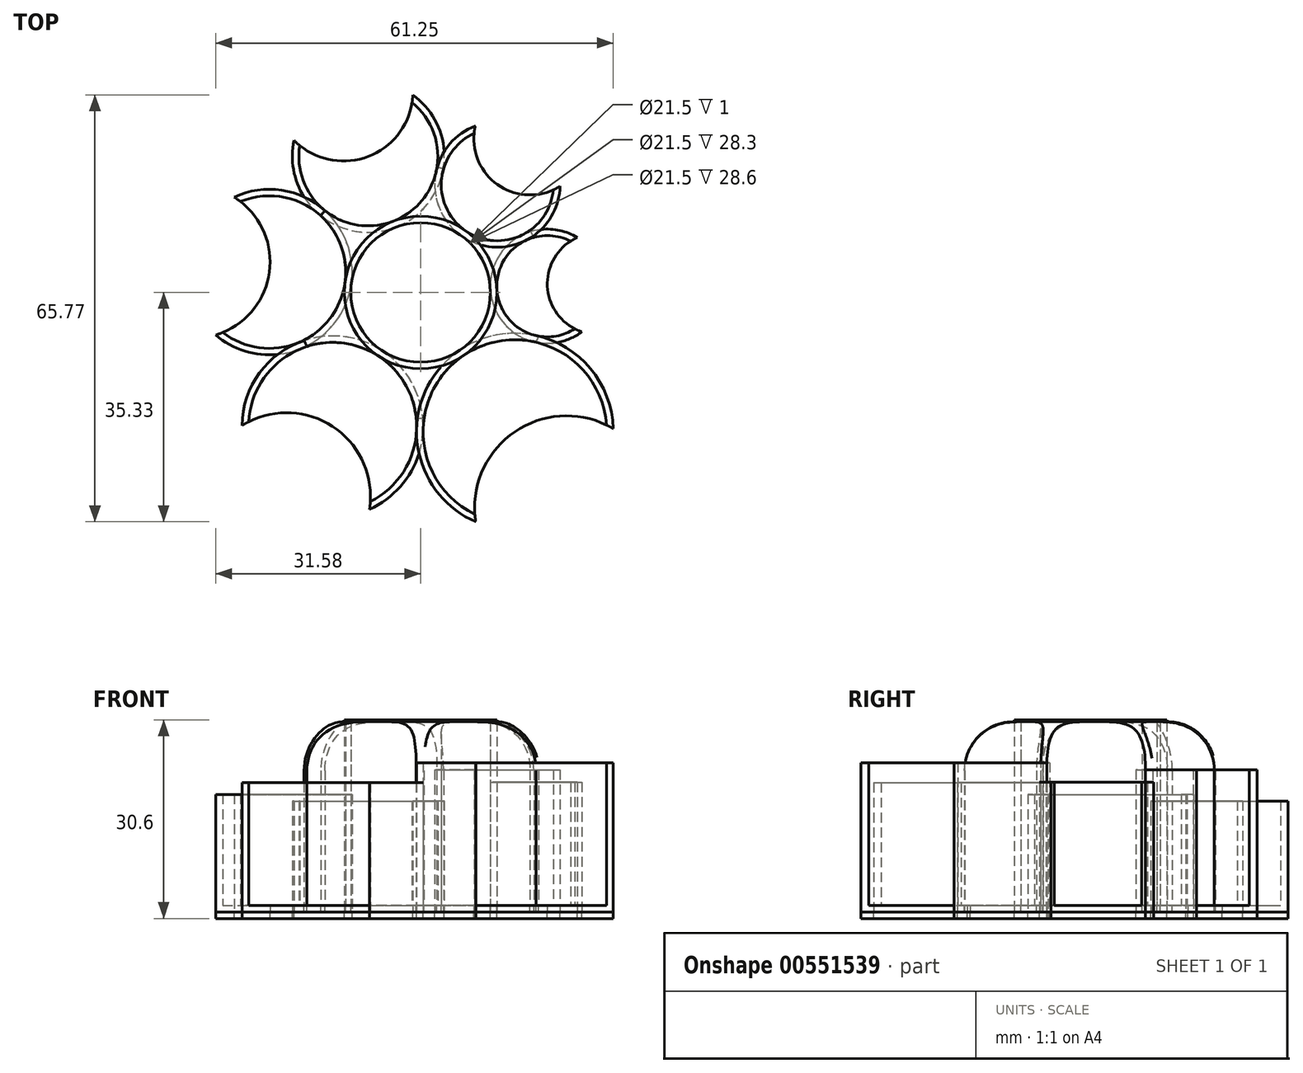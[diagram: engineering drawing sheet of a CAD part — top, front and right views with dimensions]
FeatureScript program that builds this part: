
annotation { "Feature Type Name" : "Feature", "Feature Type Description" : "" }
export const myFeature = defineFeature(function(context is Context, id is Id, definition is map)
    precondition{}
    {
        {
            var Q0;
            Q0=qCreatedBy(makeId("Top.planeOp"),FACE);
            var sketch = newSketch(context, id + "F0", { "sketchPlane" : qUnion([Q0])});
            skCircle(sketch, "E0", {"center": v(0, 0) * mm, "radius": 10.75 * mm});
            skCircle(sketch, "E1", {"center": v(14.53, -21.44) * mm, "radius": 14.15 * mm});
            skCircle(sketch, "E2", {"center": v(-13.56, -20.65) * mm, "radius": 12.95 * mm});
            skCircle(sketch, "E3", {"center": v(-23.3, 3.14) * mm, "radius": 11.75 * mm});
            skCircle(sketch, "E4", {"center": v(-8.05, 20.96) * mm, "radius": 10.7 * mm});
            skCircle(sketch, "E5", {"center": v(11.83, 16.62) * mm, "radius": 8.65 * mm});
            skCircle(sketch, "E6", {"center": v(19.53, 0.96) * mm, "radius": 7.8 * mm});
            skCircle(sketch, "E7", {"center": v(0, 0) * mm, "radius": 19.4 * mm});
            skLineSegment(sketch, "E8", {"start": v(0, 0) * mm, "end": v(14.53, -21.44) * mm, "construction": true});
            skLineSegment(sketch, "E9", {"start": v(0, 0) * mm, "end": v(19.53, 0.96) * mm, "construction": true});
            skLineSegment(sketch, "E10", {"start": v(0, 0) * mm, "end": v(11.83, 16.62) * mm, "construction": true});
            skLineSegment(sketch, "E11", {"start": v(0, 0) * mm, "end": v(-8.05, 20.96) * mm, "construction": true});
            skLineSegment(sketch, "E12", {"start": v(0, 0) * mm, "end": v(-23.3, 3.14) * mm, "construction": true});
            skLineSegment(sketch, "E13", {"start": v(0, 0) * mm, "end": v(-13.56, -20.65) * mm, "construction": true});
            skLineSegment(sketch, "E14", {"start": v(-13.56, -20.65) * mm, "end": v(-26.3, -40.07) * mm, "construction": true});
            skLineSegment(sketch, "E15", {"start": v(14.53, -21.44) * mm, "end": v(30.4, -44.87) * mm, "construction": true});
            skLineSegment(sketch, "E16", {"start": v(19.53, 0.96) * mm, "end": v(43.85, 2.15) * mm, "construction": true});
            skLineSegment(sketch, "E17", {"start": v(11.83, 16.62) * mm, "end": v(22.56, 31.7) * mm, "construction": true});
            skLineSegment(sketch, "E18", {"start": v(-8.05, 20.96) * mm, "end": v(-13.82, 35.98) * mm, "construction": true});
            skLineSegment(sketch, "E19", {"start": v(-23.3, 3.14) * mm, "end": v(-53.03, 7.14) * mm, "construction": true});
            skCircle(sketch, "E20", {"center": v(27.32, 1.34) * mm, "radius": 7.8 * mm});
            skCircle(sketch, "E21", {"center": v(16.85, 23.67) * mm, "radius": 8.65 * mm});
            skCircle(sketch, "E22", {"center": v(-11.89, 30.95) * mm, "radius": 10.7 * mm});
            skCircle(sketch, "E23", {"center": v(-34.94, 4.7) * mm, "radius": 11.75 * mm});
            skCircle(sketch, "E24", {"center": v(-20.66, -31.47) * mm, "radius": 12.95 * mm});
            skCircle(sketch, "E25", {"center": v(22.47, -33.15) * mm, "radius": 14.15 * mm});
            skSolve(sketch);
        }
        {
            var Q0;
            Q0=makeQuery(id+"F0.imprint","IMPRINT",FACE,{"disambiguationData":[TD([[makeQuery(id+"F0.imprint","IMPRINT",EDGE,{"derivedFrom":sQuery(id+"F0.wireOp",EDGE,"E6")}),1.0]])]});
            var Q1;
            {var subQ0=sQuery(id+"F0.wireOp",EDGE,"E7");var subQ1=sQuery(id+"F0.wireOp",EDGE,"E6");var subQ2=makeQuery(id+"F0.imprint","INTERSECT",VERTEX,{"disambiguationData":[OD(0.0)],"derivedFrom":[subQ1,subQ0]});Q1=makeQuery(id+"F0.imprint","IMPRINT",FACE,{"disambiguationData":[TD([[makeQuery(id+"F0.imprint","IMPRINT",EDGE,{"disambiguationData":[TD([[subQ2,-1.0]])],"derivedFrom":subQ1}),1.0]])]});}
            var Q2;
            {var subQ0=sQuery(id+"F0.wireOp",EDGE,"E20");var subQ1=sQuery(id+"F0.wireOp",EDGE,"E6");var subQ2=makeQuery(id+"F0.imprint","INTERSECT",VERTEX,{"disambiguationData":[OD(0.0)],"derivedFrom":[subQ1,subQ0]});Q2=makeQuery(id+"F0.imprint","IMPRINT",FACE,{"disambiguationData":[TD([[makeQuery(id+"F0.imprint","IMPRINT",EDGE,{"disambiguationData":[TD([[subQ2,1.0]])],"derivedFrom":subQ1}),1.0]])]});}
            extrude(context, id + "F1", {"entities" : qUnion([Q0, Q1, Q2]), "depth" : 19 * mm, "offsetDistance" : 25 * mm});
        }
        {
            var Q0;
            Q0=makeQuery(id+"F0.imprint","IMPRINT",FACE,{"disambiguationData":[TD([[makeQuery(id+"F0.imprint","IMPRINT",EDGE,{"derivedFrom":sQuery(id+"F0.wireOp",EDGE,"E5")}),1.0]])]});
            var Q1;
            {var subQ0=sQuery(id+"F0.wireOp",EDGE,"E7");var subQ1=sQuery(id+"F0.wireOp",EDGE,"E5");var subQ2=makeQuery(id+"F0.imprint","INTERSECT",VERTEX,{"disambiguationData":[OD(0.0)],"derivedFrom":[subQ1,subQ0]});Q1=makeQuery(id+"F0.imprint","IMPRINT",FACE,{"disambiguationData":[TD([[makeQuery(id+"F0.imprint","IMPRINT",EDGE,{"disambiguationData":[TD([[subQ2,-1.0]])],"derivedFrom":subQ1}),1.0]])]});}
            var Q2;
            {var subQ0=sQuery(id+"F0.wireOp",EDGE,"E21");var subQ1=sQuery(id+"F0.wireOp",EDGE,"E5");var subQ2=makeQuery(id+"F0.imprint","INTERSECT",VERTEX,{"disambiguationData":[OD(0.0)],"derivedFrom":[subQ1,subQ0]});Q2=makeQuery(id+"F0.imprint","IMPRINT",FACE,{"disambiguationData":[TD([[makeQuery(id+"F0.imprint","IMPRINT",EDGE,{"disambiguationData":[TD([[subQ2,1.0]])],"derivedFrom":subQ1}),1.0]])]});}
            extrude(context, id + "F2", {"entities" : qUnion([Q0, Q1, Q2]), "depth" : 20.9 * mm, "offsetDistance" : 25 * mm});
        }
        {
            var Q0;
            Q0=makeQuery(id+"F0.imprint","IMPRINT",FACE,{"disambiguationData":[TD([[makeQuery(id+"F0.imprint","IMPRINT",EDGE,{"derivedFrom":sQuery(id+"F0.wireOp",EDGE,"E4")}),1.0]])]});
            var Q1;
            {var subQ0=sQuery(id+"F0.wireOp",EDGE,"E7");var subQ1=sQuery(id+"F0.wireOp",EDGE,"E4");var subQ2=makeQuery(id+"F0.imprint","INTERSECT",VERTEX,{"disambiguationData":[OD(0.0)],"derivedFrom":[subQ1,subQ0]});Q1=makeQuery(id+"F0.imprint","IMPRINT",FACE,{"disambiguationData":[TD([[makeQuery(id+"F0.imprint","IMPRINT",EDGE,{"disambiguationData":[TD([[subQ2,-1.0]])],"derivedFrom":subQ1}),1.0]])]});}
            var Q2;
            {var subQ0=sQuery(id+"F0.wireOp",EDGE,"E22");var subQ1=sQuery(id+"F0.wireOp",EDGE,"E4");var subQ2=makeQuery(id+"F0.imprint","INTERSECT",VERTEX,{"disambiguationData":[OD(0.0)],"derivedFrom":[subQ1,subQ0]});Q2=makeQuery(id+"F0.imprint","IMPRINT",FACE,{"disambiguationData":[TD([[makeQuery(id+"F0.imprint","IMPRINT",EDGE,{"disambiguationData":[TD([[subQ2,1.0]])],"derivedFrom":subQ1}),1.0]])]});}
            extrude(context, id + "F3", {"entities" : qUnion([Q0, Q1, Q2]), "depth" : 16.1 * mm, "offsetDistance" : 25 * mm});
        }
        {
            var Q0;
            Q0=makeQuery(id+"F0.imprint","IMPRINT",FACE,{"disambiguationData":[TD([[makeQuery(id+"F0.imprint","IMPRINT",EDGE,{"derivedFrom":sQuery(id+"F0.wireOp",EDGE,"E3")}),1.0]])]});
            var Q1;
            {var subQ0=sQuery(id+"F0.wireOp",EDGE,"E7");var subQ1=sQuery(id+"F0.wireOp",EDGE,"E3");var subQ2=makeQuery(id+"F0.imprint","INTERSECT",VERTEX,{"disambiguationData":[OD(0.0)],"derivedFrom":[subQ1,subQ0]});Q1=makeQuery(id+"F0.imprint","IMPRINT",FACE,{"disambiguationData":[TD([[makeQuery(id+"F0.imprint","IMPRINT",EDGE,{"disambiguationData":[TD([[subQ2,1.0]])],"derivedFrom":subQ1}),1.0]])]});}
            var Q2;
            {var subQ0=sQuery(id+"F0.wireOp",EDGE,"E23");var subQ1=sQuery(id+"F0.wireOp",EDGE,"E3");var subQ2=makeQuery(id+"F0.imprint","INTERSECT",VERTEX,{"disambiguationData":[OD(0.0)],"derivedFrom":[subQ1,subQ0]});Q2=makeQuery(id+"F0.imprint","IMPRINT",FACE,{"disambiguationData":[TD([[makeQuery(id+"F0.imprint","IMPRINT",EDGE,{"disambiguationData":[TD([[subQ2,-1.0]])],"derivedFrom":subQ1}),1.0]])]});}
            extrude(context, id + "F4", {"entities" : qUnion([Q0, Q1, Q2]), "depth" : 17.1 * mm, "offsetDistance" : 25 * mm});
        }
        {
            var Q0;
            Q0=makeQuery(id+"F0.imprint","IMPRINT",FACE,{"disambiguationData":[TD([[makeQuery(id+"F0.imprint","IMPRINT",EDGE,{"derivedFrom":sQuery(id+"F0.wireOp",EDGE,"E2")}),1.0]])]});
            var Q1;
            {var subQ0=sQuery(id+"F0.wireOp",EDGE,"E7");var subQ1=sQuery(id+"F0.wireOp",EDGE,"E2");var subQ2=makeQuery(id+"F0.imprint","INTERSECT",VERTEX,{"disambiguationData":[OD(0.0)],"derivedFrom":[subQ1,subQ0]});Q1=makeQuery(id+"F0.imprint","IMPRINT",FACE,{"disambiguationData":[TD([[makeQuery(id+"F0.imprint","IMPRINT",EDGE,{"disambiguationData":[TD([[subQ2,1.0]])],"derivedFrom":subQ1}),1.0]])]});}
            var Q2;
            {var subQ0=sQuery(id+"F0.wireOp",EDGE,"E24");var subQ1=sQuery(id+"F0.wireOp",EDGE,"E2");var subQ2=makeQuery(id+"F0.imprint","INTERSECT",VERTEX,{"disambiguationData":[OD(0.0)],"derivedFrom":[subQ1,subQ0]});Q2=makeQuery(id+"F0.imprint","IMPRINT",FACE,{"disambiguationData":[TD([[makeQuery(id+"F0.imprint","IMPRINT",EDGE,{"disambiguationData":[TD([[subQ2,-1.0]])],"derivedFrom":subQ1}),1.0]])]});}
            extrude(context, id + "F5", {"entities" : qUnion([Q0, Q1, Q2]), "depth" : 18.9 * mm, "offsetDistance" : 25 * mm});
        }
        {
            var Q0;
            Q0=makeQuery(id+"F0.imprint","IMPRINT",FACE,{"disambiguationData":[TD([[makeQuery(id+"F0.imprint","IMPRINT",EDGE,{"derivedFrom":sQuery(id+"F0.wireOp",EDGE,"E1")}),1.0]])]});
            var Q1;
            {var subQ0=sQuery(id+"F0.wireOp",EDGE,"E7");var subQ1=sQuery(id+"F0.wireOp",EDGE,"E1");var subQ2=makeQuery(id+"F0.imprint","INTERSECT",VERTEX,{"disambiguationData":[OD(0.0)],"derivedFrom":[subQ1,subQ0]});Q1=makeQuery(id+"F0.imprint","IMPRINT",FACE,{"disambiguationData":[TD([[makeQuery(id+"F0.imprint","IMPRINT",EDGE,{"disambiguationData":[TD([[subQ2,-1.0]])],"derivedFrom":subQ1}),1.0]])]});}
            var Q2;
            {var subQ0=sQuery(id+"F0.wireOp",EDGE,"E25");var subQ1=sQuery(id+"F0.wireOp",EDGE,"E1");var subQ2=makeQuery(id+"F0.imprint","INTERSECT",VERTEX,{"disambiguationData":[OD(0.0)],"derivedFrom":[subQ1,subQ0]});Q2=makeQuery(id+"F0.imprint","IMPRINT",FACE,{"disambiguationData":[TD([[makeQuery(id+"F0.imprint","IMPRINT",EDGE,{"disambiguationData":[TD([[subQ2,1.0]])],"derivedFrom":subQ1}),1.0]])]});}
            extrude(context, id + "F6", {"entities" : qUnion([Q0, Q1, Q2]), "depth" : 22 * mm, "offsetDistance" : 25 * mm});
        }
        {
            var Q0;
            Q0=makeQuery(id+"F3.opExtrude","CAP_FACE",FACE,{"disambiguationData":[OSD([sQuery(id+"F0.wireOp",EDGE,"E4")])],"isStart":false});
            var Q1;
            Q1=makeQuery(id+"F4.opExtrude","CAP_FACE",FACE,{"disambiguationData":[OSD([sQuery(id+"F0.wireOp",EDGE,"E3")])],"isStart":false});
            var Q2;
            Q2=makeQuery(id+"F5.opExtrude","CAP_FACE",FACE,{"disambiguationData":[OSD([sQuery(id+"F0.wireOp",EDGE,"E2")])],"isStart":false});
            var Q3;
            Q3=makeQuery(id+"F6.opExtrude","CAP_FACE",FACE,{"disambiguationData":[OSD([sQuery(id+"F0.wireOp",EDGE,"E1")])],"isStart":false});
            var Q4;
            Q4=makeQuery(id+"F1.opExtrude","CAP_FACE",FACE,{"disambiguationData":[OSD([sQuery(id+"F0.wireOp",EDGE,"E6")])],"isStart":false});
            var Q5;
            Q5=makeQuery(id+"F2.opExtrude","CAP_FACE",FACE,{"disambiguationData":[OSD([sQuery(id+"F0.wireOp",EDGE,"E5")])],"isStart":false});
            shell(context, id + "F7", {"entities" : qUnion([Q0, Q1, Q2, Q3, Q4, Q5]), "thickness" : 1 * mm, "oppositeDirection" : true});
        }
        {
            var Q0;
            Q0=makeQuery(id+"F0.imprint","IMPRINT",FACE,{"disambiguationData":[TD([[makeQuery(id+"F0.imprint","IMPRINT",EDGE,{"derivedFrom":sQuery(id+"F0.wireOp",EDGE,"E0")}),-1.0]])]});
            extrude(context, id + "F8", {"entities" : qUnion([Q0]), "depth" : 28.3 * mm, "offsetDistance" : 25 * mm});
        }
        {
            var Q0;
            Q0=makeQuery(id+"F0.imprint","IMPRINT",FACE,{"disambiguationData":[TD([[makeQuery(id+"F0.imprint","IMPRINT",EDGE,{"derivedFrom":sQuery(id+"F0.wireOp",EDGE,"E0")}),1.0]])]});
            extrude(context, id + "F9", {"entities" : qUnion([Q0]), "depth" : 28.6 * mm, "offsetDistance" : 25 * mm});
        }
        {
            var Q0;
            Q0=makeQuery(id+"F9.opExtrude","CAP_FACE",FACE,{"disambiguationData":[OSD([sQuery(id+"F0.wireOp",EDGE,"E0")])],"isStart":false});
            shell(context, id + "F10", {"entities" : qUnion([Q0]), "thickness" : 1 * mm, "oppositeDirection" : true});
        }
        {
            var Q0;
            {var subQ0=sQuery(id+"F0.wireOp",EDGE,"E7");Q0=makeQuery(id+"F8.opExtrude","CAP_EDGE",EDGE,{"disambiguationData":[OSD([subQ0]),TDD([makeQuery(id+"F0.imprint","IMPRINT",EDGE,{"disambiguationData":[TD([[makeQuery(id+"F0.imprint","INTERSECT",VERTEX,{"disambiguationData":[OD(0.0)],"derivedFrom":[sQuery(id+"F0.wireOp",EDGE,"E5"),subQ0]}),1.0]])],"derivedFrom":subQ0})])],"isStart":false});}
            var Q1;
            {var subQ0=sQuery(id+"F0.wireOp",EDGE,"E7");Q1=makeQuery(id+"F8.opExtrude","CAP_EDGE",EDGE,{"disambiguationData":[OSD([subQ0]),TDD([makeQuery(id+"F0.imprint","IMPRINT",EDGE,{"disambiguationData":[TD([[makeQuery(id+"F0.imprint","INTERSECT",VERTEX,{"disambiguationData":[OD(0.0)],"derivedFrom":[sQuery(id+"F0.wireOp",EDGE,"E4"),subQ0]}),1.0]])],"derivedFrom":subQ0})])],"isStart":false});}
            var Q2;
            {var subQ0=sQuery(id+"F0.wireOp",EDGE,"E7");Q2=makeQuery(id+"F8.opExtrude","CAP_EDGE",EDGE,{"disambiguationData":[OSD([subQ0]),TDD([makeQuery(id+"F0.imprint","IMPRINT",EDGE,{"disambiguationData":[TD([[makeQuery(id+"F0.imprint","INTERSECT",VERTEX,{"disambiguationData":[OD(1.0)],"derivedFrom":[sQuery(id+"F0.wireOp",EDGE,"E1"),subQ0]}),-1.0]])],"derivedFrom":subQ0})])],"isStart":false});}
            var Q3;
            {var subQ0=sQuery(id+"F0.wireOp",EDGE,"E7");Q3=makeQuery(id+"F8.opExtrude","CAP_EDGE",EDGE,{"disambiguationData":[OSD([subQ0]),TDD([makeQuery(id+"F0.imprint","IMPRINT",EDGE,{"disambiguationData":[TD([[makeQuery(id+"F0.imprint","INTERSECT",VERTEX,{"disambiguationData":[OD(0.0)],"derivedFrom":[sQuery(id+"F0.wireOp",EDGE,"E1"),subQ0]}),1.0]])],"derivedFrom":subQ0})])],"isStart":false});}
            var Q4;
            {var subQ0=sQuery(id+"F0.wireOp",EDGE,"E7");Q4=makeQuery(id+"F8.opExtrude","CAP_EDGE",EDGE,{"disambiguationData":[OSD([subQ0]),TDD([makeQuery(id+"F0.imprint","IMPRINT",EDGE,{"disambiguationData":[TD([[makeQuery(id+"F0.imprint","INTERSECT",VERTEX,{"disambiguationData":[OD(0.0)],"derivedFrom":[sQuery(id+"F0.wireOp",EDGE,"E3"),subQ0]}),1.0]])],"derivedFrom":subQ0})])],"isStart":false});}
            var Q5;
            {var subQ0=sQuery(id+"F0.wireOp",EDGE,"E7");Q5=makeQuery(id+"F8.opExtrude","CAP_EDGE",EDGE,{"disambiguationData":[OSD([subQ0]),TDD([makeQuery(id+"F0.imprint","IMPRINT",EDGE,{"disambiguationData":[TD([[makeQuery(id+"F0.imprint","INTERSECT",VERTEX,{"disambiguationData":[OD(0.0)],"derivedFrom":[sQuery(id+"F0.wireOp",EDGE,"E2"),subQ0]}),1.0]])],"derivedFrom":subQ0})])],"isStart":false});}
            var Q6;
            {var subQ0=sQuery(id+"F0.wireOp",EDGE,"E7");Q6=makeQuery(id+"F8.opExtrude","CAP_EDGE",EDGE,{"disambiguationData":[OSD([subQ0]),TDD([makeQuery(id+"F0.imprint","IMPRINT",EDGE,{"disambiguationData":[TD([[makeQuery(id+"F0.imprint","INTERSECT",VERTEX,{"disambiguationData":[OD(1.0)],"derivedFrom":[sQuery(id+"F0.wireOp",EDGE,"E1"),subQ0]}),1.0]])],"derivedFrom":subQ0})])],"isStart":false});}
            var Q7;
            {var subQ0=sQuery(id+"F0.wireOp",EDGE,"E7");Q7=makeQuery(id+"F8.opExtrude","CAP_EDGE",EDGE,{"disambiguationData":[OSD([subQ0]),TDD([makeQuery(id+"F0.imprint","IMPRINT",EDGE,{"disambiguationData":[TD([[makeQuery(id+"F0.imprint","INTERSECT",VERTEX,{"disambiguationData":[OD(0.0)],"derivedFrom":[sQuery(id+"F0.wireOp",EDGE,"E1"),subQ0]}),-1.0]])],"derivedFrom":subQ0})])],"isStart":false});}
            var Q8;
            {var subQ0=sQuery(id+"F0.wireOp",EDGE,"E7");Q8=makeQuery(id+"F8.opExtrude","CAP_EDGE",EDGE,{"disambiguationData":[OSD([subQ0]),TDD([makeQuery(id+"F0.imprint","IMPRINT",EDGE,{"disambiguationData":[TD([[makeQuery(id+"F0.imprint","INTERSECT",VERTEX,{"disambiguationData":[OD(1.0)],"derivedFrom":[sQuery(id+"F0.wireOp",EDGE,"E5"),subQ0]}),1.0]])],"derivedFrom":subQ0})])],"isStart":false});}
            var Q9;
            {var subQ0=sQuery(id+"F0.wireOp",EDGE,"E7");Q9=makeQuery(id+"F8.opExtrude","CAP_EDGE",EDGE,{"disambiguationData":[OSD([subQ0]),TDD([makeQuery(id+"F0.imprint","IMPRINT",EDGE,{"disambiguationData":[TD([[makeQuery(id+"F0.imprint","INTERSECT",VERTEX,{"disambiguationData":[OD(1.0)],"derivedFrom":[sQuery(id+"F0.wireOp",EDGE,"E4"),subQ0]}),1.0]])],"derivedFrom":subQ0})])],"isStart":false});}
            fillet(context, id + "F11", {"entities" : qUnion([Q0, Q1, Q2, Q3, Q4, Q5, Q6, Q7, Q8, Q9]), "radius" : 7.5 * mm, "tangentPropagation" : true, "allowEdgeOverflow" : false});
        }
        {
            var Q0;
            {var subQ0=sQuery(id+"F0.wireOp",EDGE,"E21");var subQ1=sQuery(id+"F0.wireOp",EDGE,"E5");var subQ2=makeQuery(id+"F0.imprint","INTERSECT",VERTEX,{"disambiguationData":[OD(0.0)],"derivedFrom":[subQ1,subQ0]});Q0=makeQuery(id+"F0.imprint","IMPRINT",FACE,{"disambiguationData":[TD([[makeQuery(id+"F0.imprint","IMPRINT",EDGE,{"disambiguationData":[TD([[subQ2,1.0]])],"derivedFrom":subQ1}),1.0]])]});}
            var Q1;
            {var subQ0=sQuery(id+"F0.wireOp",EDGE,"E21");var subQ1=sQuery(id+"F0.wireOp",EDGE,"E5");var subQ2=makeQuery(id+"F0.imprint","INTERSECT",VERTEX,{"disambiguationData":[OD(0.0)],"derivedFrom":[subQ1,subQ0]});Q1=makeQuery(id+"F0.imprint","IMPRINT",FACE,{"disambiguationData":[TD([[makeQuery(id+"F0.imprint","IMPRINT",EDGE,{"disambiguationData":[TD([[subQ2,1.0]])],"derivedFrom":subQ1}),-1.0]])]});}
            extrude(context, id + "F12", {"entities" : qUnion([Q0, Q1]), "operationType" : NewBodyOperationType.REMOVE, "endBound" : BoundingType.SYMMETRIC, "depth" : 56.4 * mm, "offsetDistance" : 25 * mm});
        }
        {
            var Q0;
            {var subQ0=sQuery(id+"F0.wireOp",EDGE,"E22");var subQ1=sQuery(id+"F0.wireOp",EDGE,"E4");var subQ2=makeQuery(id+"F0.imprint","INTERSECT",VERTEX,{"disambiguationData":[OD(0.0)],"derivedFrom":[subQ1,subQ0]});Q0=makeQuery(id+"F0.imprint","IMPRINT",FACE,{"disambiguationData":[TD([[makeQuery(id+"F0.imprint","IMPRINT",EDGE,{"disambiguationData":[TD([[subQ2,1.0]])],"derivedFrom":subQ1}),-1.0]])]});}
            var Q1;
            {var subQ0=sQuery(id+"F0.wireOp",EDGE,"E22");var subQ1=sQuery(id+"F0.wireOp",EDGE,"E4");var subQ2=makeQuery(id+"F0.imprint","INTERSECT",VERTEX,{"disambiguationData":[OD(0.0)],"derivedFrom":[subQ1,subQ0]});Q1=makeQuery(id+"F0.imprint","IMPRINT",FACE,{"disambiguationData":[TD([[makeQuery(id+"F0.imprint","IMPRINT",EDGE,{"disambiguationData":[TD([[subQ2,1.0]])],"derivedFrom":subQ1}),1.0]])]});}
            extrude(context, id + "F13", {"entities" : qUnion([Q0, Q1]), "operationType" : NewBodyOperationType.REMOVE, "endBound" : BoundingType.SYMMETRIC, "depth" : 44.6 * mm, "offsetDistance" : 25 * mm});
        }
        {
            var Q0;
            {var subQ0=sQuery(id+"F0.wireOp",EDGE,"E23");var subQ1=sQuery(id+"F0.wireOp",EDGE,"E3");var subQ2=makeQuery(id+"F0.imprint","INTERSECT",VERTEX,{"disambiguationData":[OD(0.0)],"derivedFrom":[subQ1,subQ0]});Q0=makeQuery(id+"F0.imprint","IMPRINT",FACE,{"disambiguationData":[TD([[makeQuery(id+"F0.imprint","IMPRINT",EDGE,{"disambiguationData":[TD([[subQ2,-1.0]])],"derivedFrom":subQ1}),1.0]])]});}
            var Q1;
            {var subQ0=sQuery(id+"F0.wireOp",EDGE,"E23");var subQ1=sQuery(id+"F0.wireOp",EDGE,"E3");var subQ2=makeQuery(id+"F0.imprint","INTERSECT",VERTEX,{"disambiguationData":[OD(0.0)],"derivedFrom":[subQ1,subQ0]});Q1=makeQuery(id+"F0.imprint","IMPRINT",FACE,{"disambiguationData":[TD([[makeQuery(id+"F0.imprint","IMPRINT",EDGE,{"disambiguationData":[TD([[subQ2,-1.0]])],"derivedFrom":subQ1}),-1.0]])]});}
            extrude(context, id + "F14", {"entities" : qUnion([Q0, Q1]), "operationType" : NewBodyOperationType.REMOVE, "endBound" : BoundingType.SYMMETRIC, "depth" : 38.6 * mm, "offsetDistance" : 25 * mm});
        }
        {
            var Q0;
            {var subQ0=sQuery(id+"F0.wireOp",EDGE,"E24");var subQ1=sQuery(id+"F0.wireOp",EDGE,"E2");var subQ2=makeQuery(id+"F0.imprint","INTERSECT",VERTEX,{"disambiguationData":[OD(0.0)],"derivedFrom":[subQ1,subQ0]});Q0=makeQuery(id+"F0.imprint","IMPRINT",FACE,{"disambiguationData":[TD([[makeQuery(id+"F0.imprint","IMPRINT",EDGE,{"disambiguationData":[TD([[subQ2,-1.0]])],"derivedFrom":subQ1}),1.0]])]});}
            var Q1;
            {var subQ0=sQuery(id+"F0.wireOp",EDGE,"E24");var subQ1=sQuery(id+"F0.wireOp",EDGE,"E2");var subQ2=makeQuery(id+"F0.imprint","INTERSECT",VERTEX,{"disambiguationData":[OD(0.0)],"derivedFrom":[subQ1,subQ0]});Q1=makeQuery(id+"F0.imprint","IMPRINT",FACE,{"disambiguationData":[TD([[makeQuery(id+"F0.imprint","IMPRINT",EDGE,{"disambiguationData":[TD([[subQ2,-1.0]])],"derivedFrom":subQ1}),-1.0]])]});}
            extrude(context, id + "F15", {"entities" : qUnion([Q0, Q1]), "operationType" : NewBodyOperationType.REMOVE, "endBound" : BoundingType.SYMMETRIC, "depth" : 46.2 * mm, "offsetDistance" : 25 * mm});
        }
        {
            var Q0;
            {var subQ0=sQuery(id+"F0.wireOp",EDGE,"E25");var subQ1=sQuery(id+"F0.wireOp",EDGE,"E1");var subQ2=makeQuery(id+"F0.imprint","INTERSECT",VERTEX,{"disambiguationData":[OD(0.0)],"derivedFrom":[subQ1,subQ0]});Q0=makeQuery(id+"F0.imprint","IMPRINT",FACE,{"disambiguationData":[TD([[makeQuery(id+"F0.imprint","IMPRINT",EDGE,{"disambiguationData":[TD([[subQ2,1.0]])],"derivedFrom":subQ1}),1.0]])]});}
            var Q1;
            {var subQ0=sQuery(id+"F0.wireOp",EDGE,"E25");var subQ1=sQuery(id+"F0.wireOp",EDGE,"E1");var subQ2=makeQuery(id+"F0.imprint","INTERSECT",VERTEX,{"disambiguationData":[OD(0.0)],"derivedFrom":[subQ1,subQ0]});Q1=makeQuery(id+"F0.imprint","IMPRINT",FACE,{"disambiguationData":[TD([[makeQuery(id+"F0.imprint","IMPRINT",EDGE,{"disambiguationData":[TD([[subQ2,1.0]])],"derivedFrom":subQ1}),-1.0]])]});}
            extrude(context, id + "F16", {"entities" : qUnion([Q0, Q1]), "operationType" : NewBodyOperationType.REMOVE, "endBound" : BoundingType.SYMMETRIC, "depth" : 47.6 * mm, "offsetDistance" : 25 * mm});
        }
        {
            var Q0;
            {var subQ0=sQuery(id+"F0.wireOp",EDGE,"E20");var subQ1=sQuery(id+"F0.wireOp",EDGE,"E6");var subQ2=makeQuery(id+"F0.imprint","INTERSECT",VERTEX,{"disambiguationData":[OD(0.0)],"derivedFrom":[subQ1,subQ0]});Q0=makeQuery(id+"F0.imprint","IMPRINT",FACE,{"disambiguationData":[TD([[makeQuery(id+"F0.imprint","IMPRINT",EDGE,{"disambiguationData":[TD([[subQ2,1.0]])],"derivedFrom":subQ1}),1.0]])]});}
            var Q1;
            {var subQ0=sQuery(id+"F0.wireOp",EDGE,"E20");var subQ1=sQuery(id+"F0.wireOp",EDGE,"E6");var subQ2=makeQuery(id+"F0.imprint","INTERSECT",VERTEX,{"disambiguationData":[OD(0.0)],"derivedFrom":[subQ1,subQ0]});Q1=makeQuery(id+"F0.imprint","IMPRINT",FACE,{"disambiguationData":[TD([[makeQuery(id+"F0.imprint","IMPRINT",EDGE,{"disambiguationData":[TD([[subQ2,1.0]])],"derivedFrom":subQ1}),-1.0]])]});}
            extrude(context, id + "F17", {"entities" : qUnion([Q0, Q1]), "operationType" : NewBodyOperationType.REMOVE, "endBound" : BoundingType.SYMMETRIC, "depth" : 47.8 * mm, "offsetDistance" : 25 * mm});
        }
        {
            var Q0;
            Q0=makeQuery(id+"F0.imprint","IMPRINT",FACE,{"disambiguationData":[TD([[makeQuery(id+"F0.imprint","IMPRINT",EDGE,{"derivedFrom":sQuery(id+"F0.wireOp",EDGE,"E0")}),-1.0]])]});
            var Q1;
            Q1=makeQuery(id+"F5.opExtrude","CAP_FACE",FACE,{"disambiguationData":[OSD([sQuery(id+"F0.wireOp",EDGE,"E2")])],"isStart":true});
            var Q2;
            Q2=makeQuery(id+"F6.opExtrude","CAP_FACE",FACE,{"disambiguationData":[OSD([sQuery(id+"F0.wireOp",EDGE,"E1")])],"isStart":true});
            var Q3;
            Q3=makeQuery(id+"F1.opExtrude","CAP_FACE",FACE,{"disambiguationData":[OSD([sQuery(id+"F0.wireOp",EDGE,"E6")])],"isStart":true});
            var Q4;
            Q4=makeQuery(id+"F2.opExtrude","CAP_FACE",FACE,{"disambiguationData":[OSD([sQuery(id+"F0.wireOp",EDGE,"E5")])],"isStart":true});
            var Q5;
            Q5=makeQuery(id+"F3.opExtrude","CAP_FACE",FACE,{"disambiguationData":[OSD([sQuery(id+"F0.wireOp",EDGE,"E4")])],"isStart":true});
            var Q6;
            Q6=makeQuery(id+"F4.opExtrude","CAP_FACE",FACE,{"disambiguationData":[OSD([sQuery(id+"F0.wireOp",EDGE,"E3")])],"isStart":true});
            var Q7;
            Q7=makeQuery(id+"F9.opExtrude","CAP_FACE",FACE,{"disambiguationData":[OSD([sQuery(id+"F0.wireOp",EDGE,"E0")])],"isStart":true});
            extrude(context, id + "F18", {"entities" : qUnion([Q0, Q1, Q2, Q3, Q4, Q5, Q6, Q7]), "oppositeDirection" : true, "depth" : 1 * mm, "offsetDistance" : 25 * mm});
        }
    });
